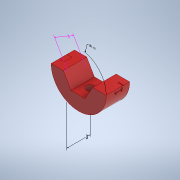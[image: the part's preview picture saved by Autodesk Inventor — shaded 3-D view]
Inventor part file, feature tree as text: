
AUTODESK INVENTOR PART (.ipt)
format: ipt  version: 2022.1 (Build 261234000, 234)  size: 741,376 bytes
history: native  units: in
note: dims shown in document units (in); Inventor stores cm internally (conversion verified against a paired STEP export)
features: other x4, sketch x4, extrude x2, thicken_offset x1, plane x1, emboss x1, hole x1, split x1
ambient origin geometry x8: Origin, YZ Plane, XZ Plane, XY Plane, X Axis, Y Axis, Z Axis, Center Point
bodies: Solid1 (feature_tree)
feature tree (15):
  other  "Annotations"
  extrude  "Extrusion1"  Depth=1.125in
  thicken_offset  "Thicken2"
  plane  "Work Plane1"
  emboss  "Emboss1"
  hole  "Hole1"  [1 undecoded]
  extrude  "Extrusion2"  Depth=0.0225in
  split  "Split1"
  sketch  "Sketch1"  dims[d0=0.5in d2=1.125in]
  sketch  "Sketch2"  dims[d3=0.2738in d4=0.5in d5=0.0in]
  sketch  "Sketch3"  dims[d8=0.0225in d9=0.0225in]
  sketch  "Sketch4"  dims[d17=1.0in d18=0.25in d19=0.1in d20=0.0in d21=0.17in d22=0.75in d23=0.5in d24=0.093in d25=0.5635in d26=0.25in d27=0.0in d28=0.2388in d29=0.2388in d30=0.191in d31=0.2186in d32=0.0in d10=0.5245in d11=1.125in d12=0.1538in d13=0.545in d14=0.1112in d15=0.3058in d16=0.4775in]
  other  "Diameter Dimension 1"
  other  "Linear Dimension 1"
  other  "Linear Dimension 2"
note: 1 required parameter value undecoded (feature->parameter linkage not recoverable at this tier; creation-order binding heuristic only, values carry confidence <= 0.55)
